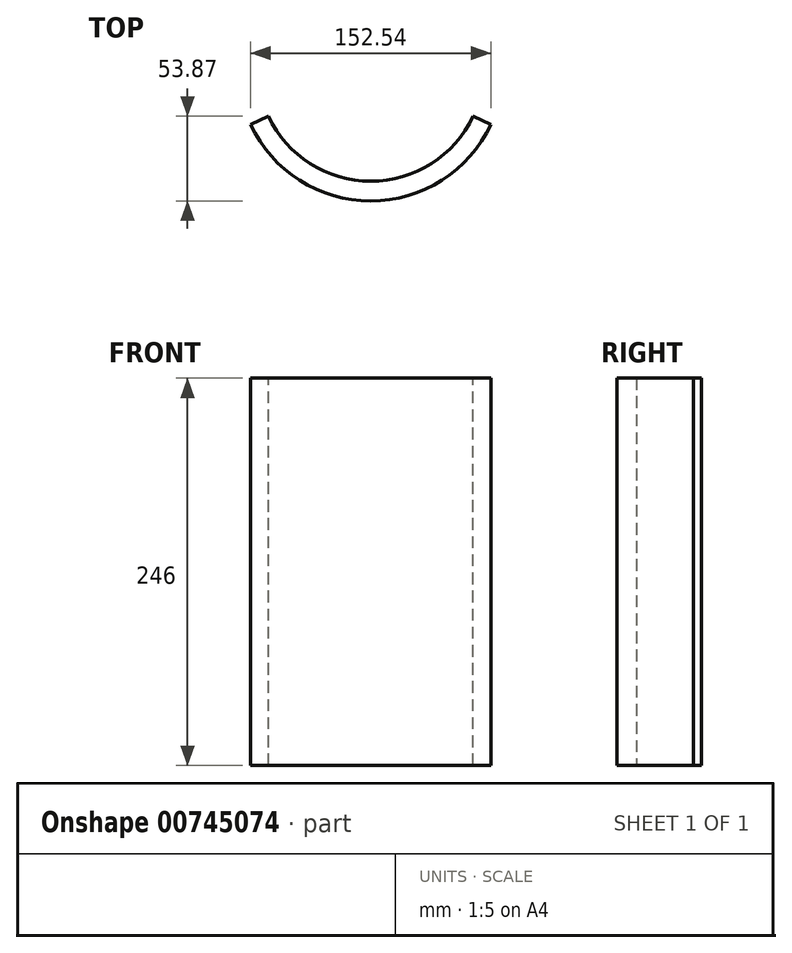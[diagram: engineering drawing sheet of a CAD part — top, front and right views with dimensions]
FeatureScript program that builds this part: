
annotation { "Feature Type Name" : "Feature", "Feature Type Description" : "" }
export const myFeature = defineFeature(function(context is Context, id is Id, definition is map)
    precondition{}
    {
        {
            var Q0;
            Q0=qCreatedBy(makeId("Top.planeOp"),FACE);
            var sketch = newSketch(context, id + "F0", { "sketchPlane" : qUnion([Q0])});
            skCircle(sketch, "E0", {"center": v(0, 0) * mm, "radius": 84.15 * mm});
            skCircle(sketch, "E1", {"center": v(0, 0) * mm, "radius": 71.65 * mm});
            skSolve(sketch);
        }
        {
            var Q0;
            Q0=makeQuery(id+"F0.imprint","IMPRINT",FACE,{"disambiguationData":[TD([[makeQuery(id+"F0.imprint","IMPRINT",EDGE,{"derivedFrom":sQuery(id+"F0.wireOp",EDGE,"E0")}),1.0]])]});
            extrude(context, id + "F1", {"entities" : qUnion([Q0]), "depth" : 246 * mm, "offsetDistance" : 25 * mm});
        }
        {
            var Q0;
            Q0=makeQuery(id+"F1.opExtrude","CAP_FACE",FACE,{"disambiguationData":[OSD([sQuery(id+"F0.wireOp",EDGE,"E0"),sQuery(id+"F0.wireOp",EDGE,"E1")])],"isStart":false});
            var sketch = newSketch(context, id + "F2", { "sketchPlane" : qUnion([Q0])});
            skLineSegment(sketch, "E2", {"start": v(0, 0) * mm, "end": v(76.27, -35.56) * mm});
            skLineSegment(sketch, "E3", {"start": v(0, 0) * mm, "end": v(-76.27, -35.56) * mm});
            skLineSegment(sketch, "E4", {"start": v(-76.27, -35.56) * mm, "end": v(76.27, -35.56) * mm});
            skSolve(sketch);
        }
        {
            var Q0;
            {var subQ1=sQuery(id+"F2.wireOp",EDGE,"E2");var subQ4=makeQuery(id+"F1.opExtrude","CAP_EDGE",EDGE,{"disambiguationData":[OSD([sQuery(id+"F0.wireOp",EDGE,"E1")])],"isStart":false});var subQ5=makeQuery(id+"F2.imprint","INTERSECT",VERTEX,{"derivedFrom":[subQ4,subQ1]});Q0=makeQuery(id+"F2.imprint","IMPRINT",FACE,{"disambiguationData":[TD([[makeQuery(id+"F2.imprint","IMPRINT",EDGE,{"disambiguationData":[TD([[subQ5,-1.0]])],"derivedFrom":subQ4}),-1.0]])]});}
            extrude(context, id + "F3", {"entities" : qUnion([Q0]), "operationType" : NewBodyOperationType.REMOVE, "endBound" : BoundingType.UP_TO_NEXT, "oppositeDirection" : true, "depth" : 25 * mm, "offsetDistance" : 25 * mm});
        }
    });
